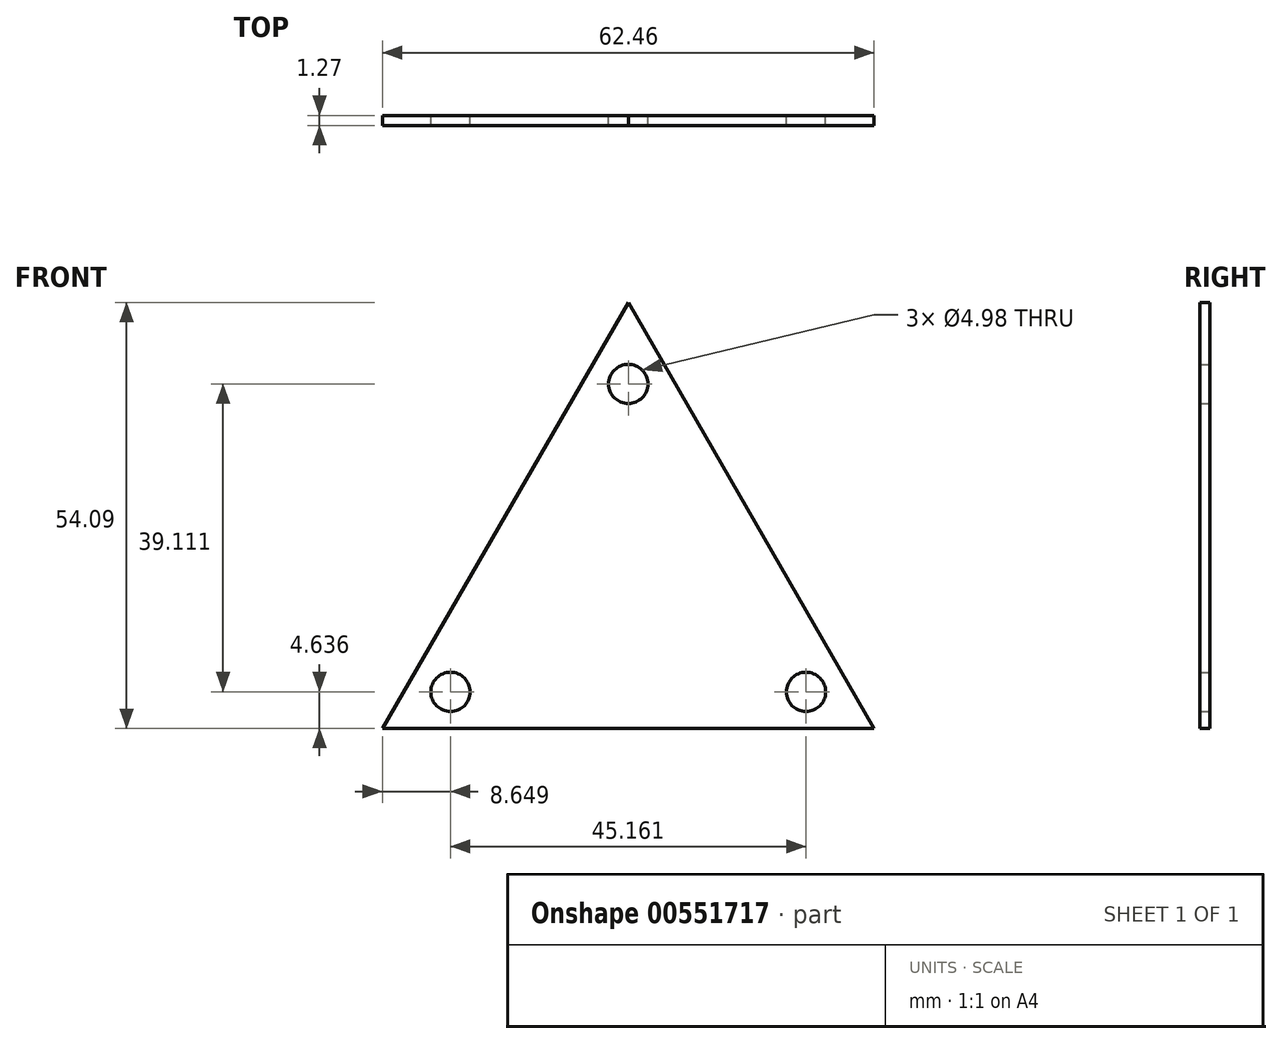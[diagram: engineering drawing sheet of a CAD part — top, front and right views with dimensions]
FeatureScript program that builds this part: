
annotation { "Feature Type Name" : "Feature", "Feature Type Description" : "" }
export const myFeature = defineFeature(function(context is Context, id is Id, definition is map)
    precondition{}
    {
        {
            var Q0;
            Q0=qCreatedBy(makeId("Front.planeOp"),FACE);
            var sketch = newSketch(context, id + "F0", { "sketchPlane" : qUnion([Q0])});
            skLineSegment(sketch, "E0", {"start": v(-31.23, 0) * mm, "end": v(31.23, 0) * mm});
            skLineSegment(sketch, "E1", {"start": v(31.23, 0) * mm, "end": v(0, 54.09) * mm});
            skLineSegment(sketch, "E2", {"start": v(0, 54.09) * mm, "end": v(-31.23, 0) * mm});
            skCircle(sketch, "E3", {"center": v(-22.58, 4.64) * mm, "radius": 2.5 * mm});
            skCircle(sketch, "E4", {"center": v(0, 43.75) * mm, "radius": 2.5 * mm});
            skCircle(sketch, "E5", {"center": v(22.58, 4.64) * mm, "radius": 2.5 * mm});
            skSolve(sketch);
        }
        {
            var Q0;
            Q0=makeQuery(id+"F0.imprint","IMPRINT",FACE,{"disambiguationData":[TD([[makeQuery(id+"F0.imprint","IMPRINT",EDGE,{"derivedFrom":sQuery(id+"F0.wireOp",EDGE,"E0")}),1.0]])]});
            extrude(context, id + "F1", {"entities" : qUnion([Q0]), "depth" : 1.27 * mm, "offsetDistance" : 25.4 * mm});
        }
    });
